# Revit family: LWplc_Latchwaysplc_FallArrestSystemGuidedAnchorLine_BUOStype
name_source: partatom
category: Generic Models
revit_build: Autodesk Revit 2014 (Build: 20130709_2115(x64)
units: mm (PartAtom-declared; Revit-internal decimal feet)

## types (6) — shared parameters
AssetType = Fixed
AttachmentDeviceGuide = www.latchways.com/BIM/Latchways_Attachment_Device_Guide.pdf
BaseCorner = 10 mm  [stored 0.0328084 ft]
Color = Dome: Stainless Steel, Electro Polished; Baseplate RAL7038
Description = Latchways ManSafe® for BUOS/ Composite Roofing, using Constant Force posts
DurationUnit = year
FireExit = No
FixingDetail = www.latchways.com/BIM/Latchways_CFP_BUOS-Composite_FixingDetail.pdf
FixingHole = 7 mm  [stored 0.0229659 ft]
Height = 195 mm  [stored 0.639764 ft]
HoleCentres = 25 mm  [stored 0.082021 ft]
HoleOffset = 13 mm
IfcExportAs = NOTDEFINED
IfcExportType = IfcTransportElement
ManSafeForRoofingBrochure = www.latchways.com/BIM/MansafeForRoofing.pdf
ManufacturerName = Latchways plc
ManufacturerURL = www.latchways.com
Material = Dome: 316s Stainless Steel; Base Plate: Aluminum Powder Coated
NBSDescription = Fall arrest system - guided anchor line
NBSReference = 80-50-25/110
NominalHeight = 195 mm  [stored 0.639764 ft]
PreInstallationSurvey = Required
ProductSpecification = www.latchways.com/BIM/Latchways_CFP_BUOS-Composite_NBS_Specification.doc
SystemMaintenance = Annual service to be completed by registered Latchways installer in accordance with BS7883:2005
SystemManufacturer = Latchways plc
URL = www.latchways.com
Uniclass2 = 80-30-25/135
Version = 1
WarrantyDurationUnit = year

## per-type parameters (varying)
| type | BIMObjectName | BasePlateLength | BasePlateWidth | BlendBaseL | BlendBaseRad | BlendBaseW | HoleVis | HoleVoid | Model | ModelNumber | ModelReference | Name | NominalLength | NominalWidth | ProductInformation | Size |
| CFP for BUOS/ Composite Roofs, 380.5 x 456 mm | LWplc_Latchwaysplc_FallArrestSystemGuidedAnchorLine_BUOStype_380.5x456mm | 240 mm | 203 mm | 42 mm  [stored 0.137795 ft] | 20 mm  [stored 0.0656168 ft] | 53 mm  [stored 0.173885 ft] | Yes | 5 mm  [stored 0.0164042 ft] | 65649-00 | 65649-00 | Constant Force Post for BUOS/ Composite Roofs, 380.5 x 456 mm | FallArrestSystemGuidedAnchorLine_BUOStype_380.5x456mm_Latchwaysplc | 481 mm | 406 mm | www.latchways.com/BIM/65649-00_LatychwaysConstantForcePost_BUOS-Comp_380.5x456.pdf | 481 x 406 x 195 mm |
| CFP for BUOS/ Composite Roofs, 300 mm | LWplc_Latchwaysplc_FallArrestSystemGuidedAnchorLine_BUOStype_300mm | 180 mm  [stored 0.590551 ft] | 163 mm  [stored 0.534777 ft] | 20 mm  [stored 0.0656168 ft] | 10 mm  [stored 0.0328084 ft] | 44 mm  [stored 0.144357 ft] | No | 1 mm  [stored 0.00328084 ft] | 65615-00 | 65615-00 | Constant Force Post for BUOS/ Composite Roofs, 300 mm | FallArrestSystemGuidedAnchorLine_BUOStype_300mm_Latchwaysplc | 359 mm  [stored 1.17782 ft] | 326 mm  [stored 1.06955 ft] | www.latchways.com/BIM/65615-00_LatchwaysConstanstForcePost_BUOS-Comp_300.pdf | 359 x 326 x 195 mm |
| CFP for BUOS/ Composite Roofs, 250 x 333 mm | LWplc_Latchwaysplc_FallArrestSystemGuidedAnchorLine_BUOStype_250x333mm | 180 mm  [stored 0.590551 ft] | 138 mm  [stored 0.452756 ft] | 20 mm  [stored 0.0656168 ft] | 20 mm  [stored 0.0656168 ft] | 20 mm  [stored 0.0656168 ft] | Yes | 5 mm  [stored 0.0164042 ft] | 65601-00 | 65601-00 | Constant Force Post for BUOS/ Composite Roofs, 250 x 333 mm | FallArrestSystemGuidedAnchorLine_BUOStype_250x333mm_Latchwaysplc | 359 mm  [stored 1.17782 ft] | 276 mm  [stored 0.905512 ft] | www.latchways.com/BIM/65601-00_LatchwaysConstantForcePost_BUOS-Comp_250x333.pdf | 359 x 276 x 195 mm |
| CFP for BUOS/ Composite Roofs, 333 x 400 mm | LWplc_Latchwaysplc_FallArrestSystemGuidedAnchorLine_BUOStype_333x400mm | 213 mm | 179 mm  [stored 0.58727 ft] | 54 mm  [stored 0.177165 ft] | 20 mm  [stored 0.0656168 ft] | 60 mm  [stored 0.19685 ft] | Yes | 5 mm  [stored 0.0164042 ft] | 65602-00 | 65602-00 | Constant Force Post for BUOS/ Composite Roofs, 333 x 400 mm | FallArrestSystemGuidedAnchorLine_BUOStype_333x400mm_Latchwaysplc | 425 mm  [stored 1.39436 ft] | 358 mm  [stored 1.17454 ft] | www.latchways.com/BIM/65602-00_LatchwaysConstantForcePost_BUOS-Comp_333x400.pdf | 425 x 358 x 195 mm |
| CFP for BUOS/ Composite Roofs, 333 x 500 mm | LWplc_Latchwaysplc_FallArrestSystemGuidedAnchorLine_BUOStype_333x500mm | 263 mm | 179 mm  [stored 0.58727 ft] | 69 mm  [stored 0.226378 ft] | 20 mm  [stored 0.0656168 ft] | 32 mm  [stored 0.104987 ft] | Yes | 5 mm  [stored 0.0164042 ft] | 65603-00 | 65603-00 | Constant Force Post for BUOS/ Composite Roofs, 333 x 500 mm | FallArrestSystemGuidedAnchorLine_BUOStype_333x500mm_Latchwaysplc | 525 mm | 358 mm  [stored 1.17454 ft] | www.latchways.com/BIM/65603-00_LatchwaysConstantForcePost_BUOS-Comp_333x500.pdf | 525 x 358 x 195 mm |
| CFP for BUOS/ Composite Roofs, 333 x 500 mm Steel | LWplc_Latchwaysplc_FallArrestSystemGuidedAnchorLine_BUOStype_Steel_333x500mm | 263 mm | 180 mm  [stored 0.590551 ft] | 69 mm  [stored 0.226378 ft] | 20 mm  [stored 0.0656168 ft] | 35 mm | Yes | 5 mm  [stored 0.0164042 ft] | 65608-00 | 65608-00 | Constant Force Post for BUOS/ Composite Roofs, 333 x 500 mm - Steel | FallArrestSystemGuidedAnchorLine_BUOStype_333x500mm-Steel_Latchwaysplc | 525 mm | 360 mm  [stored 1.1811 ft] | www.latchways.com/BIM/65608-00_LatchwaysConstantForcePost_BUOS-Comp_333x500.pdf | 525 x 360 x 195 mm |

note: [stored X ft] marks values corroborated as IEEE doubles in the binary element streams (Revit-internal decimal feet)

## geometry (parser evidence)
native form markers: Blend x3
no freeform markers — native parametric forms only
